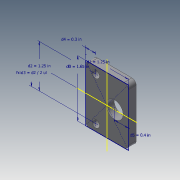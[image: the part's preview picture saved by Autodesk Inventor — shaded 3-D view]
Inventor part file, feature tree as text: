
AUTODESK INVENTOR PART (.ipt)
format: ipt  version: 2020.3 (Build 243373000, 373)  size: 120,320 bytes
history: native  units: in
note: dims shown in document units (in); Inventor stores cm internally (conversion verified against a paired STEP export)
features: hole x2, sketch x1, extrude x1, fillet x1
ambient origin geometry x8: Origin, YZ Plane, XZ Plane, XY Plane, X Axis, Y Axis, Z Axis, Center Point
bodies: Solid1 (feature_tree)
feature tree (5):
  sketch  "Sketch1"  dims[d0=1.65in d1=1.25in d2=1.25in d3=0.625in d4=0.3in d5=0.4in d6=0.23in d7=0.0in d8=0.217in d9=0.75in d10=0.394in d11=0.197in d12=90.0deg d13=1.0in d14=0.8108in d15=0.495in d16=0.75in d17=0.394in d18=0.197in d19=90.0deg d20=1.0in d21=0.8108in d22=0.125in]
  extrude  "Extrusion1"  Depth=1.25in
  hole  "Hole1"  [1 undecoded]
  hole  "Hole2"  [1 undecoded]
  fillet  "Fillet1"  Radius=0.3in
note: 2 required parameter values undecoded (feature->parameter linkage not recoverable at this tier; creation-order binding heuristic only, values carry confidence <= 0.55)
